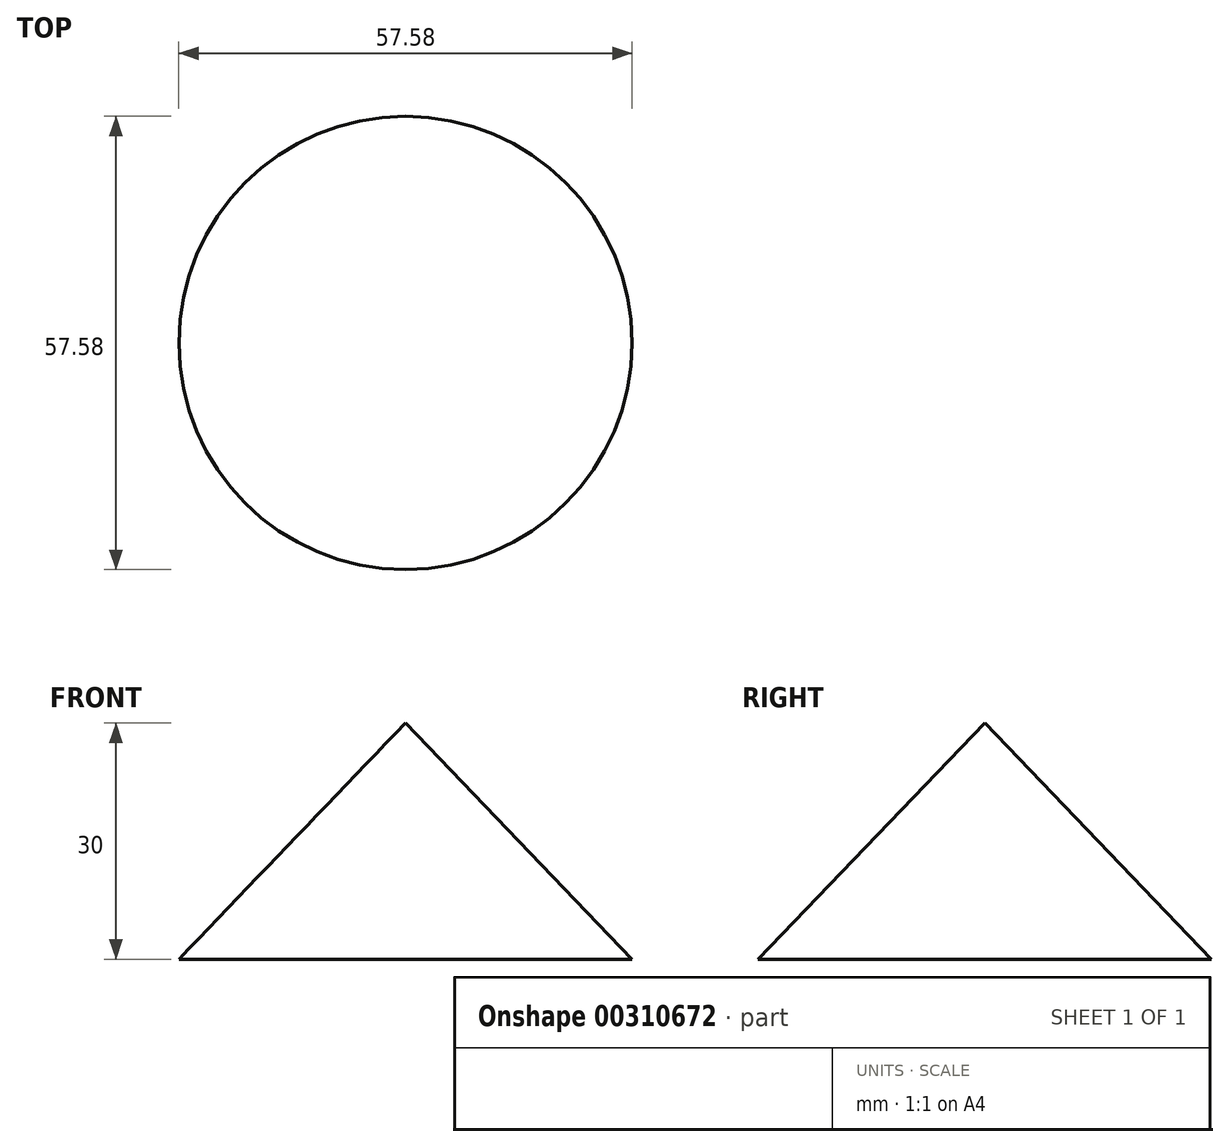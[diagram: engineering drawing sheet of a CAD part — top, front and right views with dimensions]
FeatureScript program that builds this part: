
annotation { "Feature Type Name" : "Feature", "Feature Type Description" : "" }
export const myFeature = defineFeature(function(context is Context, id is Id, definition is map)
    precondition{}
    {
        {
            var Q0;
            Q0=qCreatedBy(makeId("Front.planeOp"),FACE);
            var sketch = newSketch(context, id + "F0", { "sketchPlane" : qUnion([Q0])});
            skLineSegment(sketch, "E0", {"start": v(0, 0) * mm, "end": v(0, 30) * mm});
            skLineSegment(sketch, "E1", {"start": v(0, 30) * mm, "end": v(28.79, 0) * mm});
            skLineSegment(sketch, "E2", {"start": v(28.79, 0) * mm, "end": v(0, 0) * mm});
            skSolve(sketch);
        }
        {
            var Q0;
            Q0 = qSketchRegion(id + "F0", true);
            var Q1;
            Q1=sQuery(id+"F0.wireOp",EDGE,"E0");
            revolve(context, id + "F1", {"entities" : qUnion([Q0]), "axis" : qUnion([Q1]), "revolveType" : RevolveType.FULL});
        }
    });
